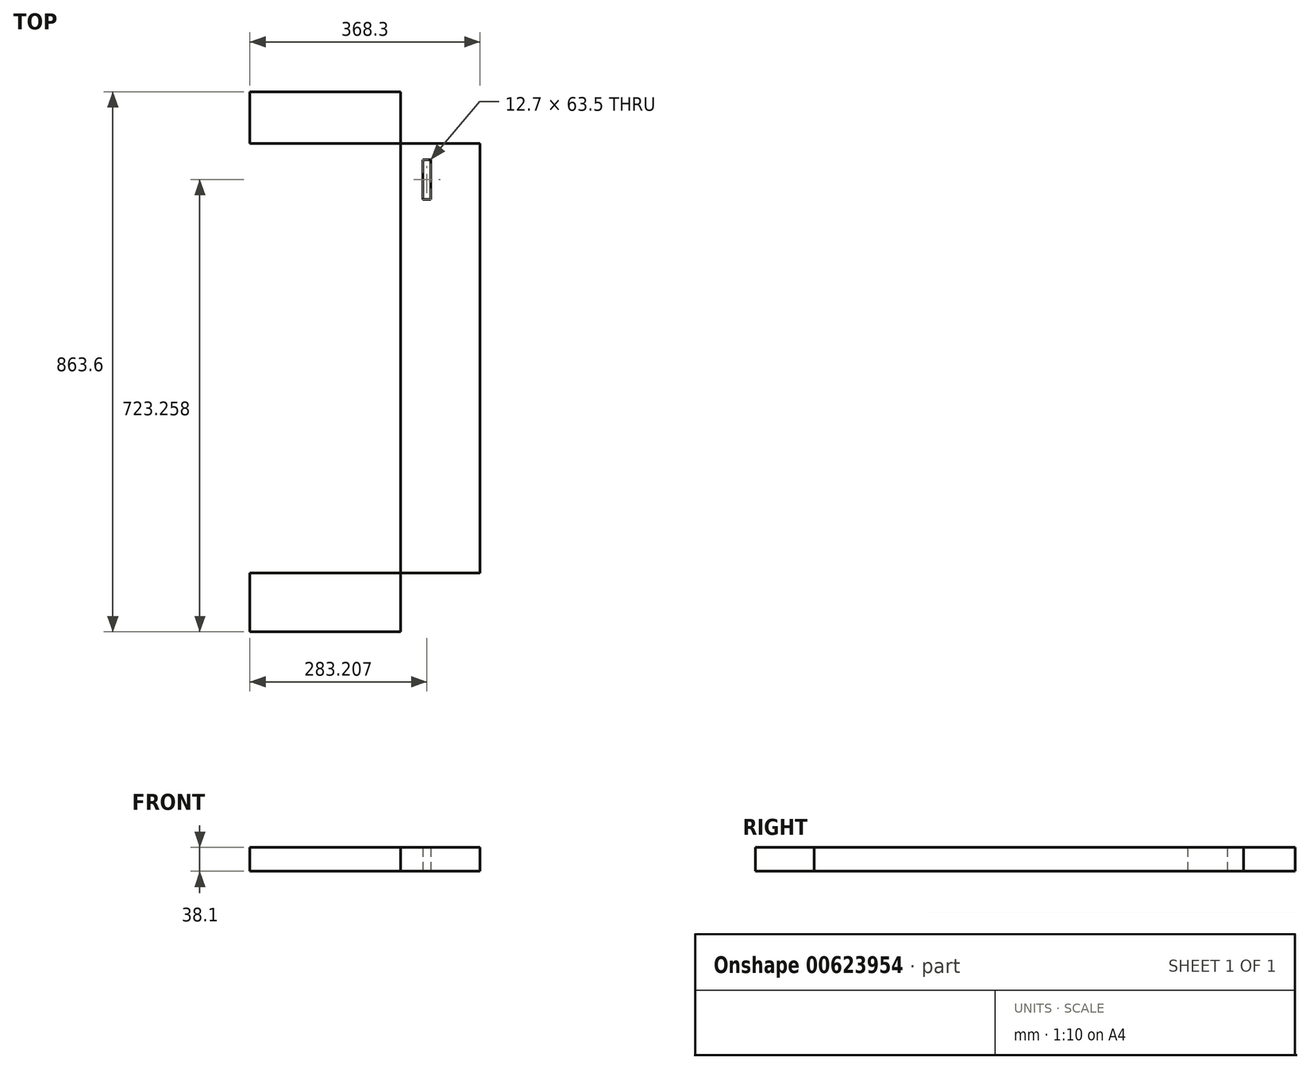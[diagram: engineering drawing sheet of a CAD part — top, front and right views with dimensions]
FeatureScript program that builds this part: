
annotation { "Feature Type Name" : "Feature", "Feature Type Description" : "" }
export const myFeature = defineFeature(function(context is Context, id is Id, definition is map)
    precondition{}
    {
        {
            var Q0;
            Q0=qCreatedBy(makeId("Top.planeOp"),FACE);
            var sketch = newSketch(context, id + "F0", { "sketchPlane" : qUnion([Q0])});
            skLineSegment(sketch, "E0.bottom", {"start": v(-122.87, 430.6) * mm, "end": v(4.13, 430.6) * mm});
            skLineSegment(sketch, "E0.top", {"start": v(-122.87, -433) * mm, "end": v(4.13, -433) * mm});
            skLineSegment(sketch, "E0.left", {"start": v(-122.87, 430.6) * mm, "end": v(-122.87, -433) * mm});
            skLineSegment(sketch, "E0.right", {"start": v(4.13, 430.6) * mm, "end": v(4.13, -433) * mm});
            skLineSegment(sketch, "E1.bottom", {"start": v(-122.87, -433) * mm, "end": v(245.43, -433) * mm});
            skLineSegment(sketch, "E1.top", {"start": v(-122.87, -339.02) * mm, "end": v(245.43, -339.02) * mm});
            skLineSegment(sketch, "E1.left", {"start": v(-122.87, -433) * mm, "end": v(-122.87, -339.02) * mm});
            skLineSegment(sketch, "E1.right", {"start": v(245.43, -433) * mm, "end": v(245.43, -339.02) * mm});
            skLineSegment(sketch, "E2.bottom", {"start": v(245.43, -433) * mm, "end": v(118.43, -433) * mm});
            skLineSegment(sketch, "E2.top", {"start": v(245.43, 430.6) * mm, "end": v(118.43, 430.6) * mm});
            skLineSegment(sketch, "E2.left", {"start": v(245.43, -433) * mm, "end": v(245.43, 430.6) * mm});
            skLineSegment(sketch, "E2.right", {"start": v(118.43, -433) * mm, "end": v(118.43, 430.6) * mm});
            skLineSegment(sketch, "E3.bottom", {"start": v(-122.87, 430.6) * mm, "end": v(245.43, 430.6) * mm});
            skLineSegment(sketch, "E3.top", {"start": v(-122.87, 347.87) * mm, "end": v(245.43, 347.87) * mm});
            skLineSegment(sketch, "E3.left", {"start": v(-122.87, 430.6) * mm, "end": v(-122.87, 347.87) * mm});
            skLineSegment(sketch, "E3.right", {"start": v(245.43, 430.6) * mm, "end": v(245.43, 347.87) * mm});
            skLineSegment(sketch, "E4.bottom", {"start": v(166.69, 322) * mm, "end": v(153.99, 322) * mm});
            skLineSegment(sketch, "E4.top", {"start": v(166.69, 258.5) * mm, "end": v(153.99, 258.5) * mm});
            skLineSegment(sketch, "E4.left", {"start": v(166.69, 322) * mm, "end": v(166.69, 258.5) * mm});
            skLineSegment(sketch, "E4.right", {"start": v(153.99, 322) * mm, "end": v(153.99, 258.5) * mm});
            skLineSegment(sketch, "E5.bottom", {"start": v(-39.05, 258.5) * mm, "end": v(-26.35, 258.5) * mm});
            skLineSegment(sketch, "E5.top", {"start": v(-39.05, 322) * mm, "end": v(-26.35, 322) * mm});
            skLineSegment(sketch, "E5.left", {"start": v(-39.05, 258.5) * mm, "end": v(-39.05, 322) * mm});
            skLineSegment(sketch, "E5.right", {"start": v(-26.35, 258.5) * mm, "end": v(-26.35, 322) * mm});
            skSolve(sketch);
        }
        {
            var Q0;
            {var subQ0=sQuery(id+"F0.wireOp",EDGE,"E0.left");Q0=makeQuery(id+"F0.imprint","IMPRINT",FACE,{"disambiguationData":[TD([[makeQuery(id+"F0.imprint","IMPRINT",EDGE,{"derivedFrom":subQ0}),1.0]])]});}
            var Q1;
            {var subQ5=sQuery(id+"F0.wireOp",EDGE,"E1.left");Q1=makeQuery(id+"F0.imprint","IMPRINT",FACE,{"disambiguationData":[TD([[makeQuery(id+"F0.imprint","IMPRINT",EDGE,{"derivedFrom":subQ5}),-1.0]])]});}
            var Q2;
            {var subQ0=sQuery(id+"F0.wireOp",EDGE,"E1.bottom");var subQ1=sQuery(id+"F0.wireOp",EDGE,"E0.right");var subQ2=makeQuery(id+"F0.imprint","INTERSECT",VERTEX,{"derivedFrom":[subQ1,subQ0]});Q2=makeQuery(id+"F0.imprint","IMPRINT",FACE,{"disambiguationData":[TD([[makeQuery(id+"F0.imprint","IMPRINT",EDGE,{"disambiguationData":[TD([[subQ2,1.0]])],"derivedFrom":subQ1}),1.0]])]});}
            var Q3;
            {var subQ5=sQuery(id+"F0.wireOp",EDGE,"E2.bottom");Q3=makeQuery(id+"F0.imprint","IMPRINT",FACE,{"disambiguationData":[TD([[makeQuery(id+"F0.imprint","IMPRINT",EDGE,{"derivedFrom":subQ5}),-1.0]])]});}
            var Q4;
            {var subQ0=sQuery(id+"F0.wireOp",EDGE,"E2.left");var subQ1=sQuery(id+"F0.wireOp",EDGE,"E1.top");var subQ2=makeQuery(id+"F0.imprint","INTERSECT",VERTEX,{"derivedFrom":[subQ1,subQ0]});Q4=makeQuery(id+"F0.imprint","IMPRINT",FACE,{"disambiguationData":[TD([[makeQuery(id+"F0.imprint","IMPRINT",EDGE,{"disambiguationData":[TD([[subQ2,1.0]])],"derivedFrom":subQ1}),1.0]])]});}
            var Q5;
            {var subQ5=sQuery(id+"F0.wireOp",EDGE,"E3.right");Q5=makeQuery(id+"F0.imprint","IMPRINT",FACE,{"disambiguationData":[TD([[makeQuery(id+"F0.imprint","IMPRINT",EDGE,{"derivedFrom":subQ5}),-1.0]])]});}
            var Q6;
            {var subQ0=sQuery(id+"F0.wireOp",EDGE,"E3.bottom");var subQ1=sQuery(id+"F0.wireOp",EDGE,"E0.right");var subQ2=makeQuery(id+"F0.imprint","INTERSECT",VERTEX,{"derivedFrom":[subQ1,subQ0]});Q6=makeQuery(id+"F0.imprint","IMPRINT",FACE,{"disambiguationData":[TD([[makeQuery(id+"F0.imprint","IMPRINT",EDGE,{"disambiguationData":[TD([[subQ2,-1.0]])],"derivedFrom":subQ1}),1.0]])]});}
            var Q7;
            {var subQ5=sQuery(id+"F0.wireOp",EDGE,"E3.left");Q7=makeQuery(id+"F0.imprint","IMPRINT",FACE,{"disambiguationData":[TD([[makeQuery(id+"F0.imprint","IMPRINT",EDGE,{"derivedFrom":subQ5}),1.0]])]});}
            extrude(context, id + "F1", {"entities" : qUnion([Q0, Q1, Q2, Q3, Q4, Q5, Q6, Q7]), "depth" : 38.1 * mm, "offsetDistance" : 25.4 * mm});
        }
    });
